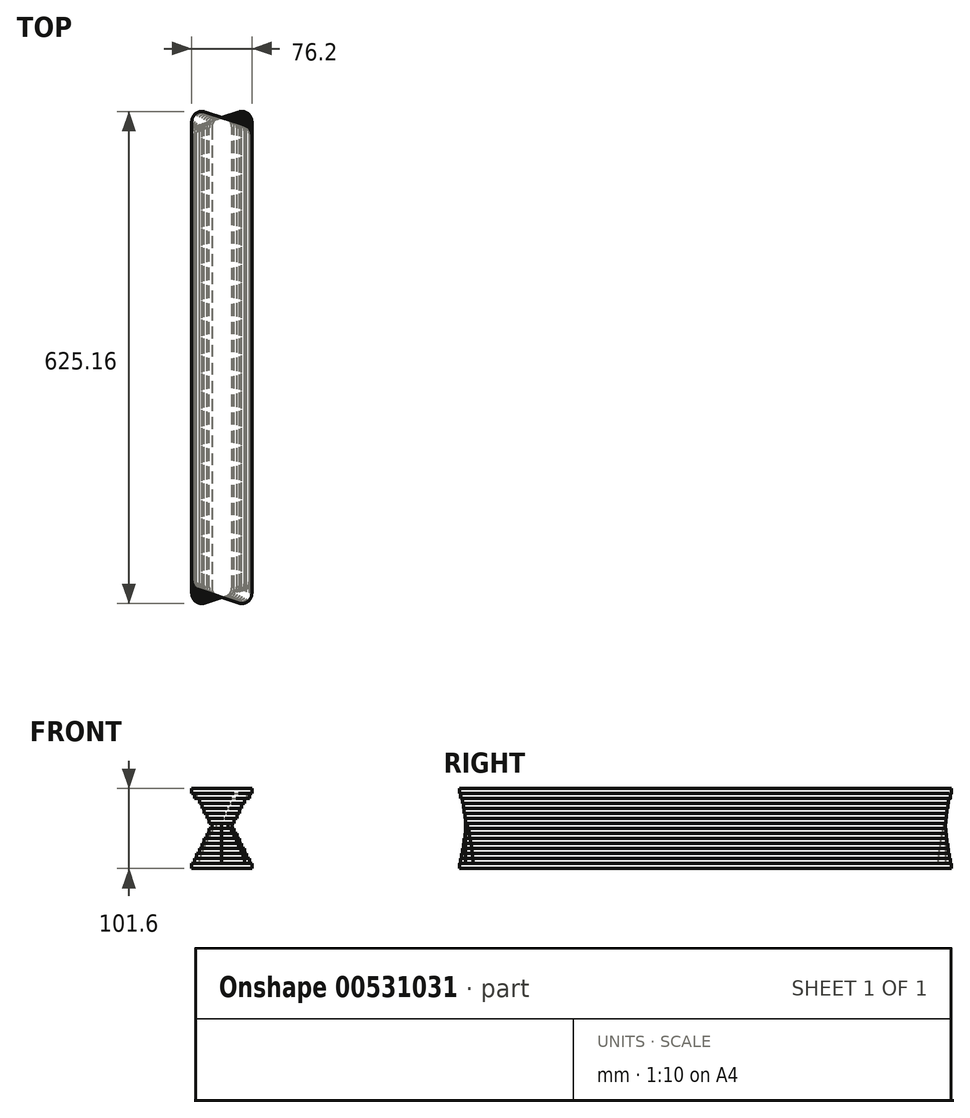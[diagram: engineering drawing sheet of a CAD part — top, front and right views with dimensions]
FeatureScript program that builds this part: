
annotation { "Feature Type Name" : "Feature", "Feature Type Description" : "" }
export const myFeature = defineFeature(function(context is Context, id is Id, definition is map)
    precondition{}
    {
        {
            var Q0;
            Q0=qCreatedBy(makeId("Top.planeOp"),FACE);
            var sketch = newSketch(context, id + "F0", { "sketchPlane" : qUnion([Q0])});
            skPoint(sketch, "E0", {"position": v(0, 0) * mm});
            skPoint(sketch, "E1", {"position": v(-38.1, 0) * mm});
            skPoint(sketch, "E2", {"position": v(-38.1, -304.8) * mm});
            skPoint(sketch, "E3", {"position": v(38.1, 0) * mm});
            skPoint(sketch, "E4", {"position": v(38.1, -279.4) * mm});
            skLineSegment(sketch, "E5", {"start": v(-38.1, 0) * mm, "end": v(-38.1, -287.18) * mm});
            skLineSegment(sketch, "E6", {"start": v(-21.38, -299.23) * mm, "end": v(29.42, -282.3) * mm});
            skLineSegment(sketch, "E7", {"start": v(38.1, -270.25) * mm, "end": v(38.1, 0) * mm});
            skArc(sketch, "E8.filletArc", {"start": v(-38.1, -287.18) * mm, "mid": v(-32.83, -297.48) * mm, "end": v(-21.38, -299.23) * mm});
            skArc(sketch, "E9.filletArc", {"start": v(29.42, -282.3) * mm, "mid": v(35.7, -277.67) * mm, "end": v(38.1, -270.25) * mm});
            skPoint(sketch, "E10", {"position": v(-38.1, 304.8) * mm});
            skPoint(sketch, "E11", {"position": v(38.1, 330.2) * mm});
            skLineSegment(sketch, "E12", {"start": v(-38.1, 0) * mm, "end": v(-38.1, 295.65) * mm});
            skLineSegment(sketch, "E13", {"start": v(-29.42, 307.7) * mm, "end": v(21.38, 324.63) * mm});
            skLineSegment(sketch, "E14", {"start": v(38.1, 312.58) * mm, "end": v(38.1, 0) * mm});
            skArc(sketch, "E15.filletArc", {"start": v(-29.42, 307.7) * mm, "mid": v(-35.7, 303.07) * mm, "end": v(-38.1, 295.65) * mm});
            skArc(sketch, "E16.filletArc", {"start": v(38.1, 312.58) * mm, "mid": v(32.83, 322.88) * mm, "end": v(21.38, 324.63) * mm});
            skSolve(sketch);
        }
        {
            var Q0;
            Q0=makeQuery(id+"F0.imprint","IMPRINT",FACE,{"disambiguationData":[TD([[makeQuery(id+"F0.imprint","IMPRINT",EDGE,{"derivedFrom":sQuery(id+"F0.wireOp",EDGE,"E5")}),1.0]])]});
            extrude(context, id + "F1", {"entities" : qUnion([Q0]), "depth" : 6.35 * mm});
        }
        {
            var Q0;
            Q0=makeQuery(id+"F1.opExtrude","CAP_FACE",FACE,{"disambiguationData":[OSD([sQuery(id+"F0.wireOp",EDGE,"E5"),sQuery(id+"F0.wireOp",EDGE,"E6"),sQuery(id+"F0.wireOp",EDGE,"E7"),sQuery(id+"F0.wireOp",EDGE,"E8.filletArc"),sQuery(id+"F0.wireOp",EDGE,"E9.filletArc"),sQuery(id+"F0.wireOp",EDGE,"E12"),sQuery(id+"F0.wireOp",EDGE,"E13"),sQuery(id+"F0.wireOp",EDGE,"E14"),sQuery(id+"F0.wireOp",EDGE,"E15.filletArc"),sQuery(id+"F0.wireOp",EDGE,"E16.filletArc")])],"isStart":false});
            var sketch = newSketch(context, id + "F2", { "sketchPlane" : qUnion([Q0])});
            skPoint(sketch, "E17", {"position": v(0, 0) * mm});
            skPoint(sketch, "E18", {"position": v(-34.93, 0) * mm});
            skPoint(sketch, "E19", {"position": v(-34.92, -303.21) * mm});
            skPoint(sketch, "E20", {"position": v(34.93, 0) * mm});
            skPoint(sketch, "E21", {"position": v(34.93, -280.99) * mm});
            skLineSegment(sketch, "E22", {"start": v(-34.93, 0) * mm, "end": v(-34.92, -285.84) * mm});
            skLineSegment(sketch, "E23", {"start": v(-18.37, -297.95) * mm, "end": v(26.08, -283.8) * mm});
            skLineSegment(sketch, "E24", {"start": v(34.93, -271.7) * mm, "end": v(34.93, 0) * mm});
            skArc(sketch, "E25.filletArc", {"start": v(-34.92, -285.84) * mm, "mid": v(-29.72, -296.1) * mm, "end": v(-18.37, -297.95) * mm});
            skArc(sketch, "E26.filletArc", {"start": v(26.08, -283.8) * mm, "mid": v(32.48, -279.2) * mm, "end": v(34.92, -271.7) * mm});
            skPoint(sketch, "E27", {"position": v(-34.93, 306.39) * mm});
            skPoint(sketch, "E28", {"position": v(34.92, 328.61) * mm});
            skLineSegment(sketch, "E29", {"start": v(-34.93, 0) * mm, "end": v(-34.93, 297.1) * mm});
            skLineSegment(sketch, "E30", {"start": v(-26.08, 309.2) * mm, "end": v(18.37, 323.35) * mm});
            skLineSegment(sketch, "E31", {"start": v(34.92, 311.24) * mm, "end": v(34.93, 0) * mm});
            skArc(sketch, "E32.filletArc", {"start": v(-26.08, 309.2) * mm, "mid": v(-32.48, 304.6) * mm, "end": v(-34.93, 297.1) * mm});
            skArc(sketch, "E33.filletArc", {"start": v(34.92, 311.24) * mm, "mid": v(29.72, 321.5) * mm, "end": v(18.37, 323.35) * mm});
            skSolve(sketch);
        }
        {
            var Q0;
            {var subQ8=sQuery(id+"F2.wireOp",EDGE,"E22");Q0=makeQuery(id+"F2.imprint","IMPRINT",FACE,{"disambiguationData":[TD([[makeQuery(id+"F2.imprint","IMPRINT",EDGE,{"derivedFrom":subQ8}),1.0]])]});}
            extrude(context, id + "F3", {"entities" : qUnion([Q0]), "depth" : 6.35 * mm});
        }
        {
            var Q0;
            Q0=makeQuery(id+"F3.opExtrude","CAP_FACE",FACE,{"disambiguationData":[OSD([sQuery(id+"F0.wireOp",EDGE,"E6"),sQuery(id+"F0.wireOp",EDGE,"E13"),sQuery(id+"F2.wireOp",EDGE,"E22"),sQuery(id+"F2.wireOp",EDGE,"E23"),sQuery(id+"F2.wireOp",EDGE,"E24"),sQuery(id+"F2.wireOp",EDGE,"E25.filletArc"),sQuery(id+"F2.wireOp",EDGE,"E26.filletArc"),sQuery(id+"F2.wireOp",EDGE,"E29"),sQuery(id+"F2.wireOp",EDGE,"E30"),sQuery(id+"F2.wireOp",EDGE,"E31"),sQuery(id+"F2.wireOp",EDGE,"E32.filletArc"),sQuery(id+"F2.wireOp",EDGE,"E33.filletArc")])],"isStart":false});
            var sketch = newSketch(context, id + "F4", { "sketchPlane" : qUnion([Q0])});
            skPoint(sketch, "E34", {"position": v(0, 0) * mm});
            skPoint(sketch, "E35", {"position": v(-31.75, 0) * mm});
            skPoint(sketch, "E36", {"position": v(-31.75, -301.63) * mm});
            skPoint(sketch, "E37", {"position": v(31.75, 0) * mm});
            skPoint(sketch, "E38", {"position": v(31.75, -282.58) * mm});
            skLineSegment(sketch, "E39", {"start": v(-31.75, 0) * mm, "end": v(-31.75, -284.56) * mm});
            skLineSegment(sketch, "E40", {"start": v(-15.4, -296.72) * mm, "end": v(22.7, -285.3) * mm});
            skLineSegment(sketch, "E41", {"start": v(31.75, -273.13) * mm, "end": v(31.75, 0) * mm});
            skArc(sketch, "E42.filletArc", {"start": v(-31.75, -284.56) * mm, "mid": v(-26.63, -294.74) * mm, "end": v(-15.4, -296.72) * mm});
            skArc(sketch, "E43.filletArc", {"start": v(22.7, -285.3) * mm, "mid": v(29.24, -280.7) * mm, "end": v(31.75, -273.13) * mm});
            skPoint(sketch, "E44.MirrorP", {"position": v(-461.86, 195.96) * mm});
            skPoint(sketch, "E45", {"position": v(-31.75, 307.98) * mm});
            skPoint(sketch, "E46", {"position": v(31.75, 327.03) * mm});
            skLineSegment(sketch, "E47", {"start": v(-31.75, 0) * mm, "end": v(-31.75, 298.53) * mm});
            skLineSegment(sketch, "E48", {"start": v(-22.7, 310.7) * mm, "end": v(15.4, 322.12) * mm});
            skLineSegment(sketch, "E49", {"start": v(31.75, 309.96) * mm, "end": v(31.75, 0) * mm});
            skArc(sketch, "E50.filletArc", {"start": v(-22.7, 310.7) * mm, "mid": v(-29.24, 306.1) * mm, "end": v(-31.75, 298.53) * mm});
            skArc(sketch, "E51.filletArc", {"start": v(31.75, 309.96) * mm, "mid": v(26.63, 320.14) * mm, "end": v(15.4, 322.12) * mm});
            skSolve(sketch);
        }
        {
            var Q0;
            {var subQ8=sQuery(id+"F4.wireOp",EDGE,"E39");Q0=makeQuery(id+"F4.imprint","IMPRINT",FACE,{"disambiguationData":[TD([[makeQuery(id+"F4.imprint","IMPRINT",EDGE,{"derivedFrom":subQ8}),1.0]])]});}
            extrude(context, id + "F5", {"entities" : qUnion([Q0]), "depth" : 6.35 * mm});
        }
        {
            var Q0;
            Q0=makeQuery(id+"F5.opExtrude","CAP_FACE",FACE,{"disambiguationData":[OSD([sQuery(id+"F0.wireOp",EDGE,"E6"),sQuery(id+"F0.wireOp",EDGE,"E13"),sQuery(id+"F4.wireOp",EDGE,"E39"),sQuery(id+"F4.wireOp",EDGE,"E40"),sQuery(id+"F4.wireOp",EDGE,"E41"),sQuery(id+"F4.wireOp",EDGE,"E42.filletArc"),sQuery(id+"F4.wireOp",EDGE,"E43.filletArc"),sQuery(id+"F4.wireOp",EDGE,"E47"),sQuery(id+"F4.wireOp",EDGE,"E48"),sQuery(id+"F4.wireOp",EDGE,"E49"),sQuery(id+"F4.wireOp",EDGE,"E50.filletArc"),sQuery(id+"F4.wireOp",EDGE,"E51.filletArc")])],"isStart":false});
            var sketch = newSketch(context, id + "F6", { "sketchPlane" : qUnion([Q0])});
            skPoint(sketch, "E52", {"position": v(0, 0) * mm});
            skPoint(sketch, "E53", {"position": v(-28.58, 0) * mm});
            skPoint(sketch, "E54", {"position": v(-28.57, -300.04) * mm});
            skPoint(sketch, "E55", {"position": v(28.58, 0) * mm});
            skPoint(sketch, "E56", {"position": v(28.58, -284.16) * mm});
            skLineSegment(sketch, "E57", {"start": v(-28.58, 0) * mm, "end": v(-28.57, -283.33) * mm});
            skLineSegment(sketch, "E58", {"start": v(-12.48, -295.57) * mm, "end": v(19.27, -286.75) * mm});
            skLineSegment(sketch, "E59", {"start": v(28.58, -274.5) * mm, "end": v(28.58, 0) * mm});
            skArc(sketch, "E60.filletArc", {"start": v(-28.57, -283.33) * mm, "mid": v(-23.56, -293.44) * mm, "end": v(-12.48, -295.57) * mm});
            skArc(sketch, "E61.filletArc", {"start": v(19.27, -286.75) * mm, "mid": v(25.99, -282.2) * mm, "end": v(28.57, -274.5) * mm});
            skPoint(sketch, "E62.MirrorP", {"position": v(-895.77, 331.85) * mm});
            skPoint(sketch, "E63", {"position": v(-28.58, 309.56) * mm});
            skPoint(sketch, "E64", {"position": v(28.57, 325.44) * mm});
            skLineSegment(sketch, "E65", {"start": v(-28.58, 0) * mm, "end": v(-28.58, 299.9) * mm});
            skLineSegment(sketch, "E66", {"start": v(-19.27, 312.15) * mm, "end": v(12.48, 320.97) * mm});
            skLineSegment(sketch, "E67", {"start": v(28.57, 308.73) * mm, "end": v(28.58, 0) * mm});
            skArc(sketch, "E68.filletArc", {"start": v(-19.27, 312.15) * mm, "mid": v(-25.99, 307.6) * mm, "end": v(-28.58, 299.9) * mm});
            skArc(sketch, "E69.filletArc", {"start": v(28.57, 308.73) * mm, "mid": v(23.56, 318.84) * mm, "end": v(12.48, 320.97) * mm});
            skSolve(sketch);
        }
        {
            var Q0;
            Q0=makeQuery(id+"F6.imprint","IMPRINT",FACE,{"disambiguationData":[TD([[makeQuery(id+"F6.imprint","IMPRINT",EDGE,{"derivedFrom":sQuery(id+"F6.wireOp",EDGE,"E57")}),1.0]])]});
            extrude(context, id + "F7", {"entities" : qUnion([Q0]), "depth" : 6.35 * mm});
        }
        {
            var Q0;
            Q0=makeQuery(id+"F7.opExtrude","CAP_FACE",FACE,{"disambiguationData":[OSD([sQuery(id+"F0.wireOp",EDGE,"E6"),sQuery(id+"F0.wireOp",EDGE,"E13"),sQuery(id+"F6.wireOp",EDGE,"E57"),sQuery(id+"F6.wireOp",EDGE,"E58"),sQuery(id+"F6.wireOp",EDGE,"E59"),sQuery(id+"F6.wireOp",EDGE,"E60.filletArc"),sQuery(id+"F6.wireOp",EDGE,"E61.filletArc"),sQuery(id+"F6.wireOp",EDGE,"E65"),sQuery(id+"F6.wireOp",EDGE,"E66"),sQuery(id+"F6.wireOp",EDGE,"E67"),sQuery(id+"F6.wireOp",EDGE,"E68.filletArc"),sQuery(id+"F6.wireOp",EDGE,"E69.filletArc")])],"isStart":false});
            var sketch = newSketch(context, id + "F8", { "sketchPlane" : qUnion([Q0])});
            skPoint(sketch, "E70", {"position": v(0, 0) * mm});
            skPoint(sketch, "E71", {"position": v(-25.4, 0) * mm});
            skPoint(sketch, "E72", {"position": v(-25.4, -298.45) * mm});
            skPoint(sketch, "E73", {"position": v(25.4, 0) * mm});
            skPoint(sketch, "E74", {"position": v(25.4, -285.75) * mm});
            skLineSegment(sketch, "E75", {"start": v(-25.4, 0) * mm, "end": v(-25.4, -282.18) * mm});
            skLineSegment(sketch, "E76", {"start": v(-9.62, -294.5) * mm, "end": v(15.78, -288.15) * mm});
            skLineSegment(sketch, "E77", {"start": v(25.4, -275.83) * mm, "end": v(25.4, 0) * mm});
            skArc(sketch, "E78.filletArc", {"start": v(-25.4, -282.18) * mm, "mid": v(-20.52, -292.2) * mm, "end": v(-9.62, -294.5) * mm});
            skArc(sketch, "E79.filletArc", {"start": v(15.78, -288.15) * mm, "mid": v(22.71, -283.65) * mm, "end": v(25.4, -275.83) * mm});
            skPoint(sketch, "E80.MirrorP", {"position": v(-1189.04, 488.26) * mm});
            skPoint(sketch, "E81", {"position": v(-25.4, 311.15) * mm});
            skPoint(sketch, "E82", {"position": v(25.4, 323.85) * mm});
            skLineSegment(sketch, "E83", {"start": v(-25.4, 0) * mm, "end": v(-25.4, 301.23) * mm});
            skLineSegment(sketch, "E84", {"start": v(-15.78, 313.55) * mm, "end": v(9.62, 319.9) * mm});
            skLineSegment(sketch, "E85", {"start": v(25.4, 307.58) * mm, "end": v(25.4, 0) * mm});
            skArc(sketch, "E86.filletArc", {"start": v(-15.78, 313.55) * mm, "mid": v(-22.71, 309.05) * mm, "end": v(-25.4, 301.23) * mm});
            skArc(sketch, "E87.filletArc", {"start": v(25.4, 307.58) * mm, "mid": v(20.52, 317.6) * mm, "end": v(9.62, 319.9) * mm});
            skSolve(sketch);
        }
        {
            var Q0;
            Q0=makeQuery(id+"F8.imprint","IMPRINT",FACE,{"disambiguationData":[TD([[makeQuery(id+"F8.imprint","IMPRINT",EDGE,{"derivedFrom":sQuery(id+"F8.wireOp",EDGE,"E75")}),1.0]])]});
            extrude(context, id + "F9", {"entities" : qUnion([Q0]), "depth" : 6.35 * mm});
        }
        {
            var Q0;
            Q0=makeQuery(id+"F9.opExtrude","CAP_FACE",FACE,{"disambiguationData":[OSD([sQuery(id+"F0.wireOp",EDGE,"E6"),sQuery(id+"F0.wireOp",EDGE,"E13"),sQuery(id+"F8.wireOp",EDGE,"E75"),sQuery(id+"F8.wireOp",EDGE,"E76"),sQuery(id+"F8.wireOp",EDGE,"E77"),sQuery(id+"F8.wireOp",EDGE,"E78.filletArc"),sQuery(id+"F8.wireOp",EDGE,"E79.filletArc"),sQuery(id+"F8.wireOp",EDGE,"E83"),sQuery(id+"F8.wireOp",EDGE,"E84"),sQuery(id+"F8.wireOp",EDGE,"E85"),sQuery(id+"F8.wireOp",EDGE,"E86.filletArc"),sQuery(id+"F8.wireOp",EDGE,"E87.filletArc")])],"isStart":false});
            var sketch = newSketch(context, id + "F10", { "sketchPlane" : qUnion([Q0])});
            skPoint(sketch, "E88", {"position": v(0, 0) * mm});
            skPoint(sketch, "E89", {"position": v(-22.23, 0) * mm});
            skPoint(sketch, "E90", {"position": v(-22.22, -296.86) * mm});
            skPoint(sketch, "E91", {"position": v(22.23, 0) * mm});
            skPoint(sketch, "E92", {"position": v(22.23, -287.34) * mm});
            skLineSegment(sketch, "E93", {"start": v(-22.23, 0) * mm, "end": v(-22.22, -281.15) * mm});
            skLineSegment(sketch, "E94", {"start": v(-6.86, -293.57) * mm, "end": v(12.19, -289.49) * mm});
            skLineSegment(sketch, "E95", {"start": v(22.23, -277.07) * mm, "end": v(22.23, 0) * mm});
            skArc(sketch, "E96.filletArc", {"start": v(-22.22, -281.15) * mm, "mid": v(-17.5, -291.03) * mm, "end": v(-6.86, -293.57) * mm});
            skArc(sketch, "E97.filletArc", {"start": v(12.19, -289.49) * mm, "mid": v(19.4, -285.05) * mm, "end": v(22.22, -277.07) * mm});
            skPoint(sketch, "E98.MirrorP", {"position": v(-1110.6, 407.11) * mm});
            skPoint(sketch, "E99", {"position": v(-22.23, 312.74) * mm});
            skPoint(sketch, "E100", {"position": v(22.22, 322.26) * mm});
            skLineSegment(sketch, "E101", {"start": v(-22.23, 0) * mm, "end": v(-22.23, 302.47) * mm});
            skLineSegment(sketch, "E102", {"start": v(-12.19, 314.89) * mm, "end": v(6.86, 318.97) * mm});
            skLineSegment(sketch, "E103", {"start": v(22.22, 306.55) * mm, "end": v(22.23, 0) * mm});
            skArc(sketch, "E104.filletArc", {"start": v(-12.19, 314.89) * mm, "mid": v(-19.4, 310.45) * mm, "end": v(-22.23, 302.47) * mm});
            skArc(sketch, "E105.filletArc", {"start": v(22.22, 306.55) * mm, "mid": v(17.5, 316.43) * mm, "end": v(6.86, 318.97) * mm});
            skSolve(sketch);
        }
        {
            var Q0;
            Q0=makeQuery(id+"F10.imprint","IMPRINT",FACE,{"disambiguationData":[TD([[makeQuery(id+"F10.imprint","IMPRINT",EDGE,{"derivedFrom":sQuery(id+"F10.wireOp",EDGE,"E93")}),1.0]])]});
            extrude(context, id + "F11", {"entities" : qUnion([Q0]), "depth" : 6.35 * mm});
        }
        {
            var Q0;
            Q0=makeQuery(id+"F11.opExtrude","CAP_FACE",FACE,{"disambiguationData":[OSD([sQuery(id+"F0.wireOp",EDGE,"E6"),sQuery(id+"F0.wireOp",EDGE,"E13"),sQuery(id+"F10.wireOp",EDGE,"E93"),sQuery(id+"F10.wireOp",EDGE,"E94"),sQuery(id+"F10.wireOp",EDGE,"E95"),sQuery(id+"F10.wireOp",EDGE,"E96.filletArc"),sQuery(id+"F10.wireOp",EDGE,"E97.filletArc"),sQuery(id+"F10.wireOp",EDGE,"E101"),sQuery(id+"F10.wireOp",EDGE,"E102"),sQuery(id+"F10.wireOp",EDGE,"E103"),sQuery(id+"F10.wireOp",EDGE,"E104.filletArc"),sQuery(id+"F10.wireOp",EDGE,"E105.filletArc")])],"isStart":false});
            var sketch = newSketch(context, id + "F12", { "sketchPlane" : qUnion([Q0])});
            skPoint(sketch, "E106", {"position": v(0, 0) * mm});
            skPoint(sketch, "E107", {"position": v(-19.05, 0) * mm});
            skPoint(sketch, "E108", {"position": v(-19.05, -295.28) * mm});
            skPoint(sketch, "E109", {"position": v(19.05, 0) * mm});
            skPoint(sketch, "E110", {"position": v(19.05, -288.93) * mm});
            skLineSegment(sketch, "E111", {"start": v(-19.05, 0) * mm, "end": v(-19.05, -280.28) * mm});
            skLineSegment(sketch, "E112", {"start": v(-4.26, -292.81) * mm, "end": v(8.44, -290.7) * mm});
            skLineSegment(sketch, "E113", {"start": v(19.05, -278.17) * mm, "end": v(19.05, 0) * mm});
            skArc(sketch, "E114.filletArc", {"start": v(-19.05, -280.28) * mm, "mid": v(-14.56, -289.97) * mm, "end": v(-4.26, -292.81) * mm});
            skArc(sketch, "E115.filletArc", {"start": v(8.44, -290.7) * mm, "mid": v(16.04, -286.38) * mm, "end": v(19.05, -278.17) * mm});
            skPoint(sketch, "E116.MirrorP", {"position": v(-1134.4, 517.38) * mm});
            skPoint(sketch, "E117", {"position": v(-19.05, 314.33) * mm});
            skPoint(sketch, "E118", {"position": v(19.05, 320.68) * mm});
            skLineSegment(sketch, "E119", {"start": v(-19.05, 0) * mm, "end": v(-19.05, 303.57) * mm});
            skLineSegment(sketch, "E120", {"start": v(-8.44, 316.1) * mm, "end": v(4.26, 318.21) * mm});
            skLineSegment(sketch, "E121", {"start": v(19.05, 305.68) * mm, "end": v(19.05, 0) * mm});
            skArc(sketch, "E122.filletArc", {"start": v(-8.44, 316.1) * mm, "mid": v(-16.04, 311.78) * mm, "end": v(-19.05, 303.57) * mm});
            skArc(sketch, "E123.filletArc", {"start": v(19.05, 305.68) * mm, "mid": v(14.56, 315.37) * mm, "end": v(4.26, 318.21) * mm});
            skSolve(sketch);
        }
        {
            var Q0;
            {var subQ12=sQuery(id+"F12.wireOp",EDGE,"E113");Q0=makeQuery(id+"F12.imprint","IMPRINT",FACE,{"disambiguationData":[TD([[makeQuery(id+"F12.imprint","IMPRINT",EDGE,{"derivedFrom":subQ12}),1.0]])]});}
            extrude(context, id + "F13", {"entities" : qUnion([Q0]), "depth" : 6.35 * mm});
        }
        {
            var Q0;
            Q0=makeQuery(id+"F13.opExtrude","CAP_FACE",FACE,{"disambiguationData":[OSD([sQuery(id+"F0.wireOp",EDGE,"E6"),sQuery(id+"F0.wireOp",EDGE,"E13"),sQuery(id+"F10.wireOp",EDGE,"E93"),sQuery(id+"F10.wireOp",EDGE,"E96.filletArc"),sQuery(id+"F10.wireOp",EDGE,"E101"),sQuery(id+"F10.wireOp",EDGE,"E102"),sQuery(id+"F10.wireOp",EDGE,"E104.filletArc"),sQuery(id+"F12.wireOp",EDGE,"E112"),sQuery(id+"F12.wireOp",EDGE,"E113"),sQuery(id+"F12.wireOp",EDGE,"E115.filletArc"),sQuery(id+"F12.wireOp",EDGE,"E121"),sQuery(id+"F12.wireOp",EDGE,"E123.filletArc")])],"isStart":false});
            var sketch = newSketch(context, id + "F14", { "sketchPlane" : qUnion([Q0])});
            skPoint(sketch, "E124", {"position": v(0, 0) * mm});
            skPoint(sketch, "E125", {"position": v(-15.88, 0) * mm});
            skPoint(sketch, "E126", {"position": v(-15.87, -293.69) * mm});
            skPoint(sketch, "E127", {"position": v(15.88, 0) * mm});
            skPoint(sketch, "E128", {"position": v(15.88, -290.51) * mm});
            skLineSegment(sketch, "E129", {"start": v(-15.88, 0) * mm, "end": v(-15.87, -279.65) * mm});
            skLineSegment(sketch, "E130", {"start": v(-1.91, -292.3) * mm, "end": v(4.44, -291.66) * mm});
            skLineSegment(sketch, "E131", {"start": v(15.88, -279.02) * mm, "end": v(15.88, 0) * mm});
            skArc(sketch, "E132.filletArc", {"start": v(-15.87, -279.65) * mm, "mid": v(-11.7, -289.07) * mm, "end": v(-1.91, -292.3) * mm});
            skArc(sketch, "E133.filletArc", {"start": v(4.44, -291.66) * mm, "mid": v(12.6, -287.54) * mm, "end": v(15.88, -279.02) * mm});
            skPoint(sketch, "E134.MirrorP", {"position": v(-1354.1, 474.43) * mm});
            skPoint(sketch, "E135", {"position": v(-15.88, 315.91) * mm});
            skPoint(sketch, "E136", {"position": v(15.87, 319.09) * mm});
            skLineSegment(sketch, "E137", {"start": v(-15.88, 0) * mm, "end": v(-15.88, 304.42) * mm});
            skLineSegment(sketch, "E138", {"start": v(-4.44, 317.06) * mm, "end": v(1.91, 317.7) * mm});
            skLineSegment(sketch, "E139", {"start": v(15.87, 305.05) * mm, "end": v(15.88, 0) * mm});
            skArc(sketch, "E140.filletArc", {"start": v(-4.44, 317.06) * mm, "mid": v(-12.6, 312.94) * mm, "end": v(-15.88, 304.42) * mm});
            skArc(sketch, "E141.filletArc", {"start": v(15.87, 305.05) * mm, "mid": v(11.7, 314.47) * mm, "end": v(1.91, 317.7) * mm});
            skSolve(sketch);
        }
        {
            var Q0;
            Q0=makeQuery(id+"F14.imprint","IMPRINT",FACE,{"disambiguationData":[TD([[makeQuery(id+"F14.imprint","IMPRINT",EDGE,{"derivedFrom":sQuery(id+"F14.wireOp",EDGE,"E129")}),1.0]])]});
            extrude(context, id + "F15", {"entities" : qUnion([Q0]), "depth" : 6.35 * mm});
        }
        {
            var Q0;
            Q0=makeQuery(id+"F15.opExtrude","CAP_FACE",FACE,{"disambiguationData":[OSD([sQuery(id+"F0.wireOp",EDGE,"E6"),sQuery(id+"F0.wireOp",EDGE,"E13"),sQuery(id+"F14.wireOp",EDGE,"E129"),sQuery(id+"F14.wireOp",EDGE,"E130"),sQuery(id+"F14.wireOp",EDGE,"E131"),sQuery(id+"F14.wireOp",EDGE,"E132.filletArc"),sQuery(id+"F14.wireOp",EDGE,"E133.filletArc"),sQuery(id+"F14.wireOp",EDGE,"E137"),sQuery(id+"F14.wireOp",EDGE,"E138"),sQuery(id+"F14.wireOp",EDGE,"E139"),sQuery(id+"F14.wireOp",EDGE,"E140.filletArc"),sQuery(id+"F14.wireOp",EDGE,"E141.filletArc")])],"isStart":false});
            var sketch = newSketch(context, id + "F16", { "sketchPlane" : qUnion([Q0])});
            skPoint(sketch, "E142", {"position": v(0, 0) * mm});
            skPoint(sketch, "E143", {"position": v(-12.7, 0) * mm});
            skPoint(sketch, "E144", {"position": v(-12.7, -292.1) * mm});
            skPoint(sketch, "E145", {"position": v(12.7, 0) * mm});
            skPoint(sketch, "E146", {"position": v(12.7, -292.1) * mm});
            skLineSegment(sketch, "E147", {"start": v(-12.7, 0) * mm, "end": v(-12.7, -279.4) * mm});
            skLineSegment(sketch, "E148", {"start": v(0, -292.1) * mm, "end": v(0, -292.1) * mm});
            skLineSegment(sketch, "E149", {"start": v(12.7, -279.4) * mm, "end": v(12.7, 0) * mm});
            skArc(sketch, "E150.filletArc", {"start": v(-12.7, -279.4) * mm, "mid": v(-8.98, -288.38) * mm, "end": v(0, -292.1) * mm});
            skArc(sketch, "E151.filletArc", {"start": v(0, -292.1) * mm, "mid": v(8.98, -288.38) * mm, "end": v(12.7, -279.4) * mm});
            skPoint(sketch, "E152.MirrorP", {"position": v(-1174.77, 259.43) * mm});
            skPoint(sketch, "E153", {"position": v(-12.7, 317.5) * mm});
            skPoint(sketch, "E154", {"position": v(12.7, 317.5) * mm});
            skLineSegment(sketch, "E155", {"start": v(-12.7, 0) * mm, "end": v(-12.7, 304.8) * mm});
            skLineSegment(sketch, "E156", {"start": v(0, 317.5) * mm, "end": v(0, 317.5) * mm});
            skLineSegment(sketch, "E157", {"start": v(12.7, 304.8) * mm, "end": v(12.7, 0) * mm});
            skArc(sketch, "E158.filletArc", {"start": v(0, 317.5) * mm, "mid": v(-8.98, 313.78) * mm, "end": v(-12.7, 304.8) * mm});
            skArc(sketch, "E159.filletArc", {"start": v(12.7, 304.8) * mm, "mid": v(8.98, 313.78) * mm, "end": v(0, 317.5) * mm});
            skSolve(sketch);
        }
        {
            var Q0;
            Q0=makeQuery(id+"F16.imprint","IMPRINT",FACE,{"disambiguationData":[TD([[makeQuery(id+"F16.imprint","IMPRINT",EDGE,{"derivedFrom":sQuery(id+"F16.wireOp",EDGE,"E147")}),1.0]])]});
            extrude(context, id + "F17", {"entities" : qUnion([Q0]), "depth" : 6.35 * mm});
        }
        {
            var Q0;
            Q0=makeQuery(id+"F17.opExtrude","CAP_FACE",FACE,{"disambiguationData":[OSD([sQuery(id+"F0.wireOp",EDGE,"E6"),sQuery(id+"F0.wireOp",EDGE,"E13"),sQuery(id+"F16.wireOp",EDGE,"E147"),sQuery(id+"F16.wireOp",EDGE,"E149"),sQuery(id+"F16.wireOp",EDGE,"E150.filletArc"),sQuery(id+"F16.wireOp",EDGE,"E151.filletArc"),sQuery(id+"F16.wireOp",EDGE,"E155"),sQuery(id+"F16.wireOp",EDGE,"E157"),sQuery(id+"F16.wireOp",EDGE,"E158.filletArc"),sQuery(id+"F16.wireOp",EDGE,"E159.filletArc")])],"isStart":false});
            var sketch = newSketch(context, id + "F18", { "sketchPlane" : qUnion([Q0])});
            skPoint(sketch, "E160", {"position": v(0, 0) * mm});
            skPoint(sketch, "E161", {"position": v(-15.88, 0) * mm});
            skPoint(sketch, "E162", {"position": v(-15.87, -290.51) * mm});
            skPoint(sketch, "E163", {"position": v(15.88, 0) * mm});
            skPoint(sketch, "E164", {"position": v(15.88, -293.69) * mm});
            skLineSegment(sketch, "E165", {"start": v(-15.88, 0) * mm, "end": v(-15.87, -279.02) * mm});
            skLineSegment(sketch, "E166", {"start": v(-4.44, -291.66) * mm, "end": v(1.91, -292.3) * mm});
            skLineSegment(sketch, "E167", {"start": v(15.88, -279.65) * mm, "end": v(15.88, 0) * mm});
            skArc(sketch, "E168.filletArc", {"start": v(-15.87, -279.02) * mm, "mid": v(-12.6, -287.54) * mm, "end": v(-4.44, -291.66) * mm});
            skArc(sketch, "E169.filletArc", {"start": v(1.91, -292.3) * mm, "mid": v(11.7, -289.07) * mm, "end": v(15.87, -279.65) * mm});
            skPoint(sketch, "E170.MirrorP", {"position": v(-1386.88, 490.35) * mm});
            skPoint(sketch, "E171", {"position": v(-15.88, 319.09) * mm});
            skPoint(sketch, "E172", {"position": v(15.87, 315.91) * mm});
            skLineSegment(sketch, "E173", {"start": v(-15.88, 0) * mm, "end": v(-15.88, 305.05) * mm});
            skLineSegment(sketch, "E174", {"start": v(-1.91, 317.7) * mm, "end": v(4.44, 317.06) * mm});
            skLineSegment(sketch, "E175", {"start": v(15.87, 304.42) * mm, "end": v(15.88, 0) * mm});
            skArc(sketch, "E176.filletArc", {"start": v(-1.91, 317.7) * mm, "mid": v(-11.7, 314.47) * mm, "end": v(-15.88, 305.05) * mm});
            skArc(sketch, "E177.filletArc", {"start": v(15.87, 304.42) * mm, "mid": v(12.6, 312.94) * mm, "end": v(4.44, 317.06) * mm});
            skSolve(sketch);
        }
        {
            var Q0;
            Q0=qSketchRegion(id+"F18",true);
            extrude(context, id + "F19", {"entities" : qUnion([Q0]), "depth" : 6.35 * mm});
        }
        {
            var Q0;
            Q0=makeQuery(id+"F19.opExtrude","CAP_FACE",FACE,{"disambiguationData":[OSD([sQuery(id+"F0.wireOp",EDGE,"E6"),sQuery(id+"F0.wireOp",EDGE,"E13"),sQuery(id+"F16.wireOp",EDGE,"E147"),sQuery(id+"F16.wireOp",EDGE,"E149"),sQuery(id+"F16.wireOp",EDGE,"E150.filletArc"),sQuery(id+"F16.wireOp",EDGE,"E151.filletArc"),sQuery(id+"F16.wireOp",EDGE,"E155"),sQuery(id+"F16.wireOp",EDGE,"E157"),sQuery(id+"F16.wireOp",EDGE,"E158.filletArc"),sQuery(id+"F16.wireOp",EDGE,"E159.filletArc"),sQuery(id+"F18.wireOp",EDGE,"E166"),sQuery(id+"F18.wireOp",EDGE,"E174")])],"isStart":false});
            var sketch = newSketch(context, id + "F20", { "sketchPlane" : qUnion([Q0])});
            skPoint(sketch, "E178", {"position": v(0, 0) * mm});
            skPoint(sketch, "E179", {"position": v(-19.05, 0) * mm});
            skPoint(sketch, "E180", {"position": v(-19.05, -288.93) * mm});
            skPoint(sketch, "E181", {"position": v(19.05, 0) * mm});
            skPoint(sketch, "E182", {"position": v(19.05, -295.28) * mm});
            skLineSegment(sketch, "E183", {"start": v(-19.05, 0) * mm, "end": v(-19.05, -278.17) * mm});
            skLineSegment(sketch, "E184", {"start": v(-8.44, -290.7) * mm, "end": v(4.26, -292.81) * mm});
            skLineSegment(sketch, "E185", {"start": v(19.05, -280.28) * mm, "end": v(19.05, 0) * mm});
            skArc(sketch, "E186.filletArc", {"start": v(-19.05, -278.17) * mm, "mid": v(-16.04, -286.38) * mm, "end": v(-8.44, -290.7) * mm});
            skArc(sketch, "E187.filletArc", {"start": v(4.26, -292.81) * mm, "mid": v(14.56, -289.97) * mm, "end": v(19.05, -280.28) * mm});
            skPoint(sketch, "E188.MirrorP", {"position": v(-2251.33, 639) * mm});
            skPoint(sketch, "E189", {"position": v(-19.05, 320.68) * mm});
            skPoint(sketch, "E190", {"position": v(19.05, 314.33) * mm});
            skLineSegment(sketch, "E191", {"start": v(-19.05, 0) * mm, "end": v(-19.05, 305.68) * mm});
            skLineSegment(sketch, "E192", {"start": v(-4.26, 318.21) * mm, "end": v(8.44, 316.1) * mm});
            skLineSegment(sketch, "E193", {"start": v(19.05, 303.57) * mm, "end": v(19.05, 0) * mm});
            skArc(sketch, "E194.filletArc", {"start": v(-4.26, 318.21) * mm, "mid": v(-14.56, 315.37) * mm, "end": v(-19.05, 305.68) * mm});
            skArc(sketch, "E195.filletArc", {"start": v(19.05, 303.57) * mm, "mid": v(16.04, 311.78) * mm, "end": v(8.44, 316.1) * mm});
            skSolve(sketch);
        }
        {
            var Q0;
            Q0=qSketchRegion(id+"F20",true);
            extrude(context, id + "F21", {"entities" : qUnion([Q0]), "depth" : 6.35 * mm});
        }
        {
            var Q0;
            Q0=makeQuery(id+"F21.opExtrude","CAP_FACE",FACE,{"disambiguationData":[OSD([sQuery(id+"F0.wireOp",EDGE,"E6"),sQuery(id+"F0.wireOp",EDGE,"E13"),sQuery(id+"F16.wireOp",EDGE,"E147"),sQuery(id+"F16.wireOp",EDGE,"E149"),sQuery(id+"F16.wireOp",EDGE,"E150.filletArc"),sQuery(id+"F16.wireOp",EDGE,"E151.filletArc"),sQuery(id+"F16.wireOp",EDGE,"E155"),sQuery(id+"F16.wireOp",EDGE,"E157"),sQuery(id+"F16.wireOp",EDGE,"E158.filletArc"),sQuery(id+"F16.wireOp",EDGE,"E159.filletArc"),sQuery(id+"F20.wireOp",EDGE,"E184"),sQuery(id+"F20.wireOp",EDGE,"E192")])],"isStart":false});
            var sketch = newSketch(context, id + "F22", { "sketchPlane" : qUnion([Q0])});
            skPoint(sketch, "E196", {"position": v(0, 0) * mm});
            skPoint(sketch, "E197", {"position": v(-22.23, 0) * mm});
            skPoint(sketch, "E198", {"position": v(-22.22, -287.34) * mm});
            skPoint(sketch, "E199", {"position": v(22.23, 0) * mm});
            skPoint(sketch, "E200", {"position": v(22.23, -296.86) * mm});
            skLineSegment(sketch, "E201", {"start": v(-22.23, 0) * mm, "end": v(-22.22, -277.07) * mm});
            skLineSegment(sketch, "E202", {"start": v(-12.19, -289.49) * mm, "end": v(6.86, -293.57) * mm});
            skLineSegment(sketch, "E203", {"start": v(22.23, -281.15) * mm, "end": v(22.23, 0) * mm});
            skArc(sketch, "E204.filletArc", {"start": v(-22.22, -277.07) * mm, "mid": v(-19.4, -285.05) * mm, "end": v(-12.19, -289.49) * mm});
            skArc(sketch, "E205.filletArc", {"start": v(6.86, -293.57) * mm, "mid": v(17.5, -291.03) * mm, "end": v(22.22, -281.15) * mm});
            skPoint(sketch, "E206.MirrorP", {"position": v(-2054.65, 833.78) * mm});
            skPoint(sketch, "E207", {"position": v(-22.23, 322.26) * mm});
            skPoint(sketch, "E208", {"position": v(22.22, 312.74) * mm});
            skLineSegment(sketch, "E209", {"start": v(-22.23, 0) * mm, "end": v(-22.23, 306.55) * mm});
            skLineSegment(sketch, "E210", {"start": v(-6.86, 318.97) * mm, "end": v(12.19, 314.89) * mm});
            skLineSegment(sketch, "E211", {"start": v(22.22, 302.47) * mm, "end": v(22.23, 0) * mm});
            skArc(sketch, "E212.filletArc", {"start": v(-6.86, 318.97) * mm, "mid": v(-17.5, 316.43) * mm, "end": v(-22.23, 306.55) * mm});
            skArc(sketch, "E213.filletArc", {"start": v(22.22, 302.47) * mm, "mid": v(19.4, 310.45) * mm, "end": v(12.19, 314.89) * mm});
            skSolve(sketch);
        }
        {
            var Q0;
            Q0=qSketchRegion(id+"F22",true);
            extrude(context, id + "F23", {"entities" : qUnion([Q0]), "depth" : 6.35 * mm});
        }
        {
            var Q0;
            Q0=makeQuery(id+"F23.opExtrude","CAP_FACE",FACE,{"disambiguationData":[OSD([sQuery(id+"F22.wireOp",EDGE,"E201"),sQuery(id+"F22.wireOp",EDGE,"E202"),sQuery(id+"F22.wireOp",EDGE,"E203"),sQuery(id+"F22.wireOp",EDGE,"E204.filletArc"),sQuery(id+"F22.wireOp",EDGE,"E205.filletArc"),sQuery(id+"F22.wireOp",EDGE,"E209"),sQuery(id+"F22.wireOp",EDGE,"E210"),sQuery(id+"F22.wireOp",EDGE,"E211"),sQuery(id+"F22.wireOp",EDGE,"E212.filletArc"),sQuery(id+"F22.wireOp",EDGE,"E213.filletArc")])],"isStart":false});
            var sketch = newSketch(context, id + "F24", { "sketchPlane" : qUnion([Q0])});
            skPoint(sketch, "E214", {"position": v(0, 0) * mm});
            skPoint(sketch, "E215", {"position": v(-25.4, 0) * mm});
            skPoint(sketch, "E216", {"position": v(-25.4, -285.75) * mm});
            skPoint(sketch, "E217", {"position": v(25.4, 0) * mm});
            skPoint(sketch, "E218", {"position": v(25.4, -298.45) * mm});
            skLineSegment(sketch, "E219", {"start": v(-25.4, 0) * mm, "end": v(-25.4, -275.83) * mm});
            skLineSegment(sketch, "E220", {"start": v(-15.78, -288.15) * mm, "end": v(9.62, -294.5) * mm});
            skLineSegment(sketch, "E221", {"start": v(25.4, -282.18) * mm, "end": v(25.4, 0) * mm});
            skArc(sketch, "E222.filletArc", {"start": v(-25.4, -275.83) * mm, "mid": v(-22.71, -283.65) * mm, "end": v(-15.78, -288.15) * mm});
            skArc(sketch, "E223.filletArc", {"start": v(9.62, -294.5) * mm, "mid": v(20.52, -292.2) * mm, "end": v(25.4, -282.18) * mm});
            skPoint(sketch, "E224.MirrorP", {"position": v(-1763.83, 631.7) * mm});
            skPoint(sketch, "E225", {"position": v(-25.4, 323.85) * mm});
            skPoint(sketch, "E226", {"position": v(25.4, 311.15) * mm});
            skLineSegment(sketch, "E227", {"start": v(-25.4, 0) * mm, "end": v(-25.4, 307.58) * mm});
            skLineSegment(sketch, "E228", {"start": v(-9.62, 319.9) * mm, "end": v(15.78, 313.55) * mm});
            skLineSegment(sketch, "E229", {"start": v(25.4, 301.23) * mm, "end": v(25.4, 0) * mm});
            skArc(sketch, "E230.filletArc", {"start": v(-9.62, 319.9) * mm, "mid": v(-20.52, 317.6) * mm, "end": v(-25.4, 307.58) * mm});
            skArc(sketch, "E231.filletArc", {"start": v(25.4, 301.23) * mm, "mid": v(22.71, 309.05) * mm, "end": v(15.78, 313.55) * mm});
            skSolve(sketch);
        }
        {
            var Q0;
            Q0=qSketchRegion(id+"F24",true);
            extrude(context, id + "F25", {"entities" : qUnion([Q0]), "depth" : 6.35 * mm});
        }
        {
            var Q0;
            Q0=makeQuery(id+"F25.opExtrude","CAP_FACE",FACE,{"disambiguationData":[OSD([sQuery(id+"F24.wireOp",EDGE,"E219"),sQuery(id+"F24.wireOp",EDGE,"E220"),sQuery(id+"F24.wireOp",EDGE,"E221"),sQuery(id+"F24.wireOp",EDGE,"E222.filletArc"),sQuery(id+"F24.wireOp",EDGE,"E223.filletArc"),sQuery(id+"F24.wireOp",EDGE,"E227"),sQuery(id+"F24.wireOp",EDGE,"E228"),sQuery(id+"F24.wireOp",EDGE,"E229"),sQuery(id+"F24.wireOp",EDGE,"E230.filletArc"),sQuery(id+"F24.wireOp",EDGE,"E231.filletArc")])],"isStart":false});
            var sketch = newSketch(context, id + "F26", { "sketchPlane" : qUnion([Q0])});
            skPoint(sketch, "E232", {"position": v(0, 0) * mm});
            skPoint(sketch, "E233", {"position": v(-28.58, 0) * mm});
            skPoint(sketch, "E234", {"position": v(-28.57, -284.16) * mm});
            skPoint(sketch, "E235", {"position": v(28.58, 0) * mm});
            skPoint(sketch, "E236", {"position": v(28.58, -300.04) * mm});
            skLineSegment(sketch, "E237", {"start": v(-28.58, 0) * mm, "end": v(-28.57, -274.5) * mm});
            skLineSegment(sketch, "E238", {"start": v(-19.27, -286.75) * mm, "end": v(12.48, -295.57) * mm});
            skLineSegment(sketch, "E239", {"start": v(28.58, -283.33) * mm, "end": v(28.58, 0) * mm});
            skArc(sketch, "E240.filletArc", {"start": v(-28.57, -274.5) * mm, "mid": v(-25.99, -282.2) * mm, "end": v(-19.27, -286.75) * mm});
            skArc(sketch, "E241.filletArc", {"start": v(12.48, -295.57) * mm, "mid": v(23.56, -293.44) * mm, "end": v(28.57, -283.33) * mm});
            skPoint(sketch, "E242.MirrorP", {"position": v(-2122.86, 677.9) * mm});
            skPoint(sketch, "E243", {"position": v(-28.58, 325.44) * mm});
            skPoint(sketch, "E244", {"position": v(28.57, 309.56) * mm});
            skLineSegment(sketch, "E245", {"start": v(-28.58, 0) * mm, "end": v(-28.58, 308.73) * mm});
            skLineSegment(sketch, "E246", {"start": v(-12.48, 320.97) * mm, "end": v(19.27, 312.15) * mm});
            skLineSegment(sketch, "E247", {"start": v(28.57, 299.9) * mm, "end": v(28.58, 0) * mm});
            skArc(sketch, "E248.filletArc", {"start": v(-12.48, 320.97) * mm, "mid": v(-23.56, 318.84) * mm, "end": v(-28.58, 308.73) * mm});
            skArc(sketch, "E249.filletArc", {"start": v(28.57, 299.9) * mm, "mid": v(25.99, 307.6) * mm, "end": v(19.27, 312.15) * mm});
            skSolve(sketch);
        }
        {
            var Q0;
            Q0=qSketchRegion(id+"F26",true);
            extrude(context, id + "F27", {"entities" : qUnion([Q0]), "depth" : 6.35 * mm});
        }
        {
            var Q0;
            Q0=makeQuery(id+"F27.opExtrude","CAP_FACE",FACE,{"disambiguationData":[OSD([sQuery(id+"F26.wireOp",EDGE,"E237"),sQuery(id+"F26.wireOp",EDGE,"E238"),sQuery(id+"F26.wireOp",EDGE,"E239"),sQuery(id+"F26.wireOp",EDGE,"E240.filletArc"),sQuery(id+"F26.wireOp",EDGE,"E241.filletArc"),sQuery(id+"F26.wireOp",EDGE,"E245"),sQuery(id+"F26.wireOp",EDGE,"E246"),sQuery(id+"F26.wireOp",EDGE,"E247"),sQuery(id+"F26.wireOp",EDGE,"E248.filletArc"),sQuery(id+"F26.wireOp",EDGE,"E249.filletArc")])],"isStart":false});
            var sketch = newSketch(context, id + "F28", { "sketchPlane" : qUnion([Q0])});
            skPoint(sketch, "E250", {"position": v(0, 0) * mm});
            skPoint(sketch, "E251", {"position": v(-31.75, 0) * mm});
            skPoint(sketch, "E252", {"position": v(-31.75, -282.58) * mm});
            skPoint(sketch, "E253", {"position": v(31.75, 0) * mm});
            skPoint(sketch, "E254", {"position": v(31.75, -301.63) * mm});
            skLineSegment(sketch, "E255", {"start": v(-31.75, 0) * mm, "end": v(-31.75, -273.13) * mm});
            skLineSegment(sketch, "E256", {"start": v(-22.7, -285.3) * mm, "end": v(15.4, -296.72) * mm});
            skLineSegment(sketch, "E257", {"start": v(31.75, -284.56) * mm, "end": v(31.75, 0) * mm});
            skArc(sketch, "E258.filletArc", {"start": v(-31.75, -273.13) * mm, "mid": v(-29.24, -280.7) * mm, "end": v(-22.7, -285.3) * mm});
            skArc(sketch, "E259.filletArc", {"start": v(15.4, -296.72) * mm, "mid": v(26.63, -294.74) * mm, "end": v(31.75, -284.56) * mm});
            skPoint(sketch, "E260.MirrorP", {"position": v(-2131.05, 728.59) * mm});
            skPoint(sketch, "E261", {"position": v(-31.75, 327.03) * mm});
            skPoint(sketch, "E262", {"position": v(31.75, 307.98) * mm});
            skLineSegment(sketch, "E263", {"start": v(-31.75, 0) * mm, "end": v(-31.75, 309.96) * mm});
            skLineSegment(sketch, "E264", {"start": v(-15.4, 322.12) * mm, "end": v(22.7, 310.7) * mm});
            skLineSegment(sketch, "E265", {"start": v(31.75, 298.53) * mm, "end": v(31.75, 0) * mm});
            skArc(sketch, "E266.filletArc", {"start": v(-15.4, 322.12) * mm, "mid": v(-26.63, 320.14) * mm, "end": v(-31.75, 309.96) * mm});
            skArc(sketch, "E267.filletArc", {"start": v(31.75, 298.53) * mm, "mid": v(29.24, 306.1) * mm, "end": v(22.7, 310.7) * mm});
            skSolve(sketch);
        }
        {
            var Q0;
            Q0=qSketchRegion(id+"F28",true);
            extrude(context, id + "F29", {"entities" : qUnion([Q0]), "depth" : 6.35 * mm});
        }
        {
            var Q0;
            {var subQ12=makeQuery(id+"F27.opExtrude","CAP_EDGE",EDGE,{"disambiguationData":[OSD([sQuery(id+"F26.wireOp",EDGE,"E241.filletArc")])],"isStart":false});Q0=makeQuery(id+"F28.imprint","IMPRINT",FACE,{"disambiguationData":[TD([[makeQuery(id+"F28.imprint","IMPRINT",EDGE,{"derivedFrom":subQ12}),1.0]])]});}
            var sketch = newSketch(context, id + "F30", { "sketchPlane" : qUnion([Q0])});
            skPoint(sketch, "E268", {"position": v(0, 0) * mm});
            skPoint(sketch, "E269", {"position": v(-34.93, 0) * mm});
            skPoint(sketch, "E270", {"position": v(-34.93, -280.99) * mm});
            skPoint(sketch, "E271", {"position": v(34.93, 0) * mm});
            skPoint(sketch, "E272", {"position": v(34.93, -303.21) * mm});
            skLineSegment(sketch, "E273", {"start": v(-34.93, 0) * mm, "end": v(-34.93, -271.7) * mm});
            skLineSegment(sketch, "E274", {"start": v(-26.08, -283.8) * mm, "end": v(18.37, -297.95) * mm});
            skLineSegment(sketch, "E275", {"start": v(34.93, -285.84) * mm, "end": v(34.93, 0) * mm});
            skArc(sketch, "E276.filletArc", {"start": v(-34.93, -271.7) * mm, "mid": v(-32.48, -279.2) * mm, "end": v(-26.08, -283.8) * mm});
            skArc(sketch, "E277.filletArc", {"start": v(18.37, -297.95) * mm, "mid": v(29.72, -296.1) * mm, "end": v(34.92, -285.84) * mm});
            skPoint(sketch, "E278.MirrorP", {"position": v(-2087.8, 736.08) * mm});
            skPoint(sketch, "E279", {"position": v(-34.93, 328.61) * mm});
            skPoint(sketch, "E280", {"position": v(34.92, 306.39) * mm});
            skLineSegment(sketch, "E281", {"start": v(-34.93, 0) * mm, "end": v(-34.93, 311.24) * mm});
            skLineSegment(sketch, "E282", {"start": v(-18.37, 323.35) * mm, "end": v(26.08, 309.2) * mm});
            skLineSegment(sketch, "E283", {"start": v(34.92, 297.1) * mm, "end": v(34.93, 0) * mm});
            skArc(sketch, "E284.filletArc", {"start": v(-18.37, 323.35) * mm, "mid": v(-29.72, 321.5) * mm, "end": v(-34.93, 311.24) * mm});
            skArc(sketch, "E285.filletArc", {"start": v(34.92, 297.1) * mm, "mid": v(32.48, 304.6) * mm, "end": v(26.08, 309.2) * mm});
            skSolve(sketch);
        }
        {
            var Q0;
            Q0=qSketchRegion(id+"F30",true);
            extrude(context, id + "F31", {"entities" : qUnion([Q0]), "depth" : 6.35 * mm});
        }
        {
            var Q0;
            Q0=makeQuery(id+"F31.opExtrude","CAP_FACE",FACE,{"disambiguationData":[OSD([sQuery(id+"F30.wireOp",EDGE,"E273"),sQuery(id+"F30.wireOp",EDGE,"E274"),sQuery(id+"F30.wireOp",EDGE,"E275"),sQuery(id+"F30.wireOp",EDGE,"E276.filletArc"),sQuery(id+"F30.wireOp",EDGE,"E277.filletArc"),sQuery(id+"F30.wireOp",EDGE,"E281"),sQuery(id+"F30.wireOp",EDGE,"E282"),sQuery(id+"F30.wireOp",EDGE,"E283"),sQuery(id+"F30.wireOp",EDGE,"E284.filletArc"),sQuery(id+"F30.wireOp",EDGE,"E285.filletArc")])],"isStart":false});
            var sketch = newSketch(context, id + "F32", { "sketchPlane" : qUnion([Q0])});
            skPoint(sketch, "E286", {"position": v(0, 0) * mm});
            skPoint(sketch, "E287", {"position": v(-38.1, 0) * mm});
            skPoint(sketch, "E288", {"position": v(-38.1, -279.4) * mm});
            skPoint(sketch, "E289", {"position": v(38.1, 0) * mm});
            skPoint(sketch, "E290", {"position": v(38.1, -304.8) * mm});
            skLineSegment(sketch, "E291", {"start": v(-38.1, 0) * mm, "end": v(-38.1, -270.25) * mm});
            skLineSegment(sketch, "E292", {"start": v(-29.42, -282.3) * mm, "end": v(21.38, -299.23) * mm});
            skLineSegment(sketch, "E293", {"start": v(38.1, -287.18) * mm, "end": v(38.1, 0) * mm});
            skArc(sketch, "E294.filletArc", {"start": v(-38.1, -270.25) * mm, "mid": v(-35.7, -277.67) * mm, "end": v(-29.42, -282.3) * mm});
            skArc(sketch, "E295.filletArc", {"start": v(21.38, -299.23) * mm, "mid": v(32.83, -297.48) * mm, "end": v(38.1, -287.18) * mm});
            skPoint(sketch, "E296.MirrorP", {"position": v(-2058.68, 783.5) * mm});
            skPoint(sketch, "E297", {"position": v(-38.1, 330.2) * mm});
            skPoint(sketch, "E298", {"position": v(38.1, 304.8) * mm});
            skLineSegment(sketch, "E299", {"start": v(-38.1, 0) * mm, "end": v(-38.1, 312.58) * mm});
            skLineSegment(sketch, "E300", {"start": v(-21.38, 324.63) * mm, "end": v(29.42, 307.7) * mm});
            skLineSegment(sketch, "E301", {"start": v(38.1, 295.65) * mm, "end": v(38.1, 0) * mm});
            skArc(sketch, "E302.filletArc", {"start": v(-21.38, 324.63) * mm, "mid": v(-32.83, 322.88) * mm, "end": v(-38.1, 312.58) * mm});
            skArc(sketch, "E303.filletArc", {"start": v(38.1, 295.65) * mm, "mid": v(35.7, 303.07) * mm, "end": v(29.42, 307.7) * mm});
            skSolve(sketch);
        }
        {
            var Q0;
            Q0=qSketchRegion(id+"F32",true);
            extrude(context, id + "F33", {"entities" : qUnion([Q0]), "depth" : 6.35 * mm});
        }
    });
